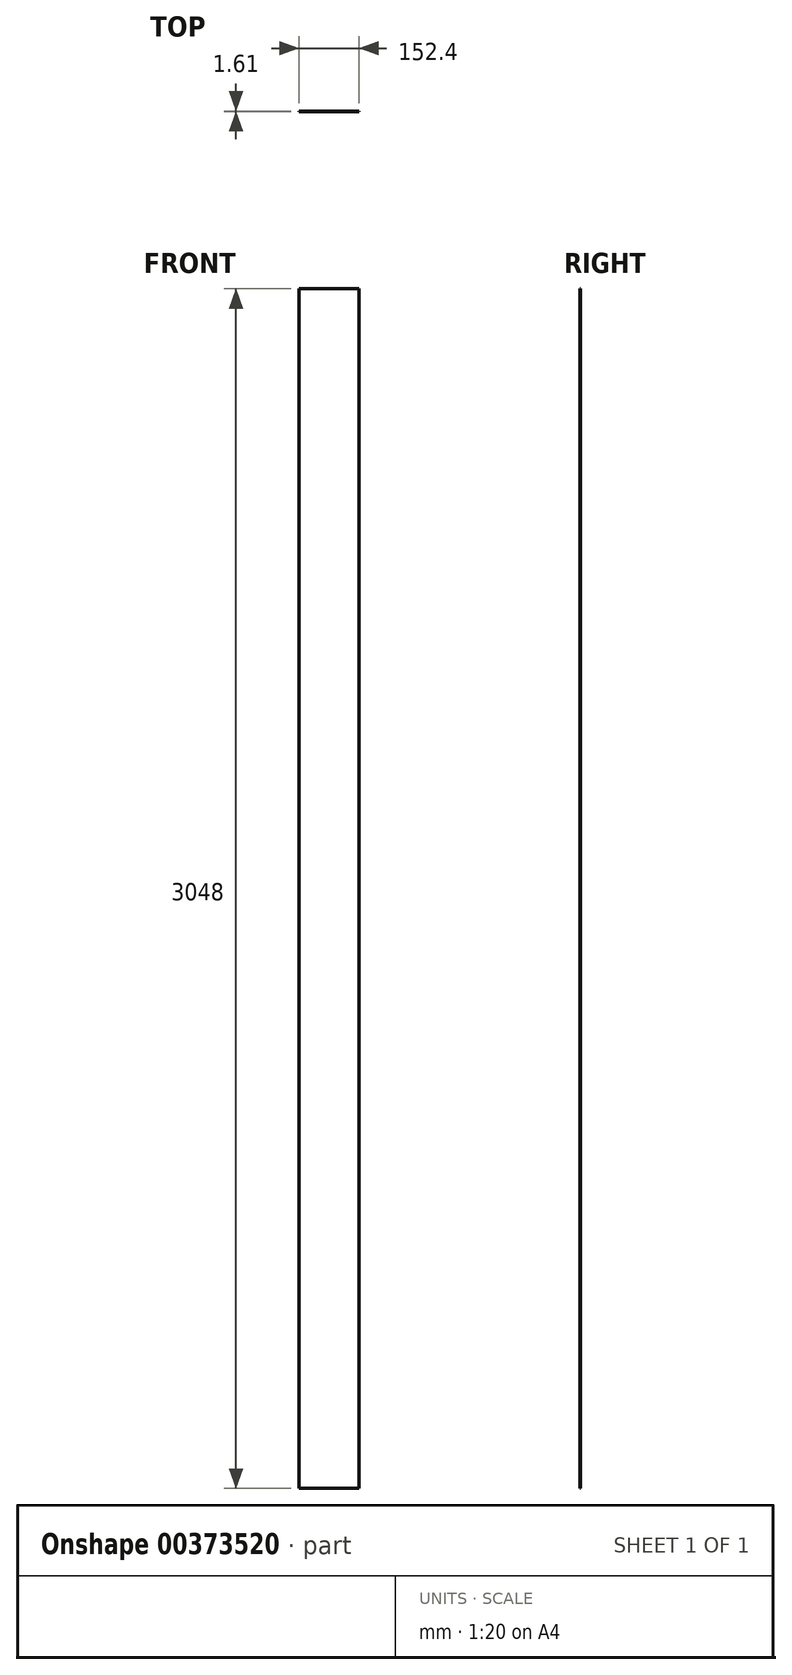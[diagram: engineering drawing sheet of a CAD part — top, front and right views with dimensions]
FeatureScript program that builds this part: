
annotation { "Feature Type Name" : "Feature", "Feature Type Description" : "" }
export const myFeature = defineFeature(function(context is Context, id is Id, definition is map)
    precondition{}
    {
        {
            var Q0;
            Q0=qCreatedBy(makeId("Front.planeOp"),FACE);
            var sketch = newSketch(context, id + "F0", { "sketchPlane" : qUnion([Q0])});
            skLineSegment(sketch, "E0.bottom", {"start": v(-22.99, 2994.24) * mm, "end": v(129.41, 2994.24) * mm});
            skLineSegment(sketch, "E0.top", {"start": v(-22.99, -53.76) * mm, "end": v(129.41, -53.76) * mm});
            skLineSegment(sketch, "E0.left", {"start": v(-22.99, 2994.24) * mm, "end": v(-22.99, -53.76) * mm});
            skLineSegment(sketch, "E0.right", {"start": v(129.41, 2994.24) * mm, "end": v(129.41, -53.76) * mm});
            skSolve(sketch);
        }
        {
            var Q0;
            Q0=makeQuery(id+"F0.imprint","IMPRINT",FACE,{"disambiguationData":[TD([[makeQuery(id+"F0.imprint","IMPRINT",EDGE,{"derivedFrom":sQuery(id+"F0.wireOp",EDGE,"E0.bottom")}),-1.0]])]});
            extrude(context, id + "F1", {"entities" : qUnion([Q0]), "depth" : 1.61 * mm});
        }
    });
